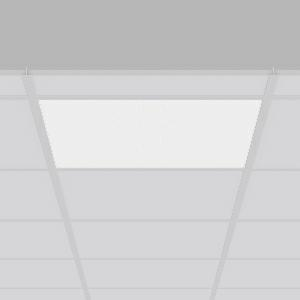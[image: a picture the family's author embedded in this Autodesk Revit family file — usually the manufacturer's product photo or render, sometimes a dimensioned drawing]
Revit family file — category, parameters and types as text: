
# Revit family: parledo_312603_002_76_10d1
name_source: partatom
category: Lighting Fixtures
units: mm (PartAtom-declared; Revit-internal decimal feet)

## family parameters
Cut with Voids When Loaded = No
Host = Face
Light Source = No
Part Type = Normal
Room Calculation Point = No
Round Connector Dimension = Use Diameter
Shared = No

## types (1)
- PARLEDO (1 x LED Modul 940, 4050 lm, 4000)
    Apparent Load = 32 VA
    CIE Flux Codes = 63 90 99 100 100
    Color Rendering = 92
    Color Temperature = 4000
    Default Elevation = 1800 mm
    Description = Series: PARLEDO
Highly efficient LED lay-in ceiling luminaire for high hygienic requirements. Particularly suitable for use in healthcare and industry. Housing: sheet steel, powder-coated. Frameless appearance in the modular ceiling thanks to the extra slim frame. Luminaire frame: aluminium, powder-coated. Diffuser with smooth surface on the room side for low sensitivity to dirt and easy cleaning. Diffuser made of resistant polycarbonate (PC), microprismatic. LED backlight technology for homogeneous illumination of the entire light-emitting surface. Excellent light quality for clinical detection of cyanosis thanks to correct colour spectrum, CRI >90 and a Cyanosis Observation Index (COI) of <3.3. External driver. Easy to install thanks to extended connection cable (2 m). IoT-ready. Suitable for through wiring as standard. Protection type IP 65 for luminaire and control gear on room and ceiling side. Perfect for office areas (RUG < 19) and environments with computer screens in accordance with EN 12464-1. Qualified for use in the food and drink industry. 
Colour: white
Length: 622 mm
Width: 622 mm
Cut-out length: 600 mm
Cut-out width: 600 mm
Recess height: 160 mm
Luminaire: recess height: 41 mm
Lamp: LED
Socket: without socket
Colour temperature: 4000K
Colour rendering index (CRI): 90
System power: 32 W
Rated luminous flux: 4050 lm
Luminous efficiency: 127 lm/W
Control gear: Converter, dimmable, DALI
Protection class: I
Type of protection: IP 65
    Height = 0 mm  [stored 0 ft]
    Lamp = 1 x LED Modul 940
    Lamp Light Flux = 4050 lm
    Lamp count = 1
    Length = 622 mm
    Lifetime = 50000 h
    Luminous efficacy = 127 lm/W
    Manufacturer = RZB
    ModVariant = No
    Model = 312603.002.76
    Mounting Place = Ceiling
    Mounting Type = Recessed
    Number of Poles = 1
    OnlyDefault = Yes
    Power Factor = 1
    Product Name = PARLEDO
    Product group = Recessed modular luminaires
    ProductGroupID = 406
    Protection Class = Protection class I
    Protection Degree = IP 65
    RLX_Detail_Level = 1
    RLX_Emergency_Light_Flux = 0 lm
    RLX_Emergency_Type = 0
    RLX_Emergency_Type_DB = No
    RlxData = <blob elided: 26629 chars, md5=1349a029>
    Socket = socket
    Standby Power = 0 W
    System Light Flux = 4050 lm
    System Power = 32 W
    Type Comments = Product without accessories
    Type Image = 312577.002.76.jpg
    URL = http://relux.com
    VarID = ---
    Voltage = 0 V
    Weight = 0.00 kg
    Width = 622 mm

note: [stored X ft] marks values corroborated as IEEE doubles in the binary element streams (Revit-internal decimal feet)

## geometry (parser evidence)
native form markers: Blend x4, Sweep x12
no freeform markers — native parametric forms only
